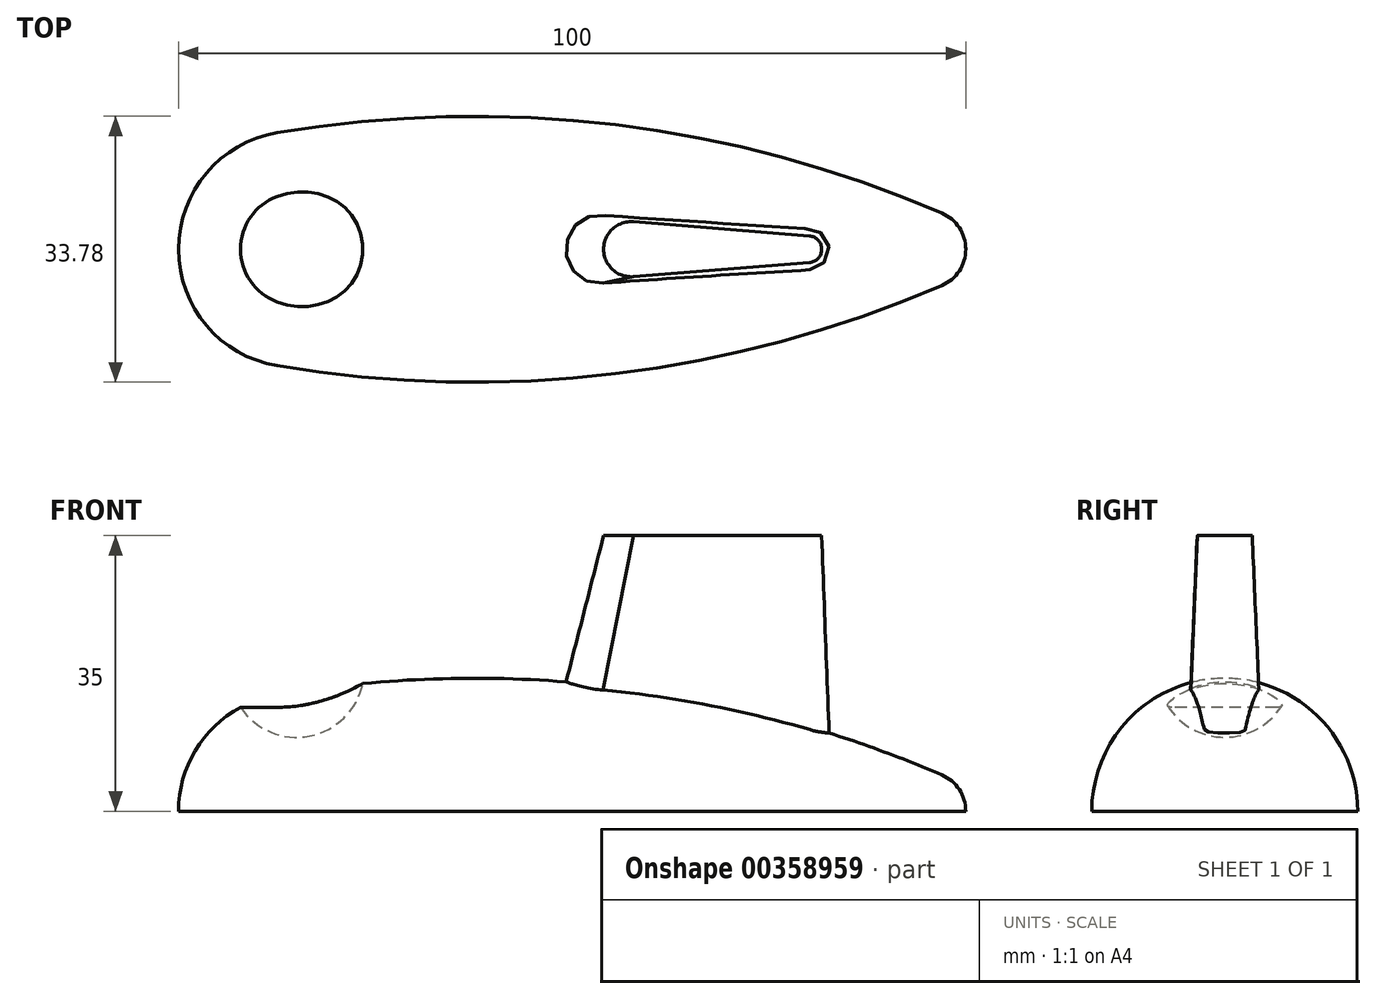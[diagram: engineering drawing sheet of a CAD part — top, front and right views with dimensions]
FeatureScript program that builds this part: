
annotation { "Feature Type Name" : "Feature", "Feature Type Description" : "" }
export const myFeature = defineFeature(function(context is Context, id is Id, definition is map)
    precondition{}
    {
        {
            var Q0;
            Q0=qCreatedBy(makeId("Top.planeOp"),FACE);
            var sketch = newSketch(context, id + "F0", { "sketchPlane" : qUnion([Q0])});
            skArc(sketch, "E0", {"start": v(-2.5, 14.8) * mm, "mid": v(-11.46, 9.68) * mm, "end": v(-15, 0) * mm});
            skArc(sketch, "E1", {"start": v(85, 0) * mm, "mid": v(84.18, 2.75) * mm, "end": v(81.98, 4.6) * mm});
            skArc(sketch, "E2", {"start": v(81.98, 4.6) * mm, "mid": v(40.48, 15.8) * mm, "end": v(-2.5, 14.8) * mm});
            skLineSegment(sketch, "E3", {"start": v(-15, 0) * mm, "end": v(85, 0) * mm});
            skPoint(sketch, "E4.orphan", {"position": v(-20.4, 0) * mm});
            skSolve(sketch);
        }
        {
            var Q0;
            Q0=makeQuery(id+"F0.imprint","IMPRINT",FACE,{"disambiguationData":[TD([[makeQuery(id+"F0.imprint","IMPRINT",EDGE,{"derivedFrom":sQuery(id+"F0.wireOp",EDGE,"E0")}),1.0]])]});
            var Q1;
            Q1=sQuery(id+"F0.wireOp",EDGE,"E3");
            revolve(context, id + "F1", {"entities" : qUnion([Q0]), "axis" : qUnion([Q1]), "revolveType" : RevolveType.ONE_DIRECTION, "angle" : 180 * degree});
        }
        {
            var Q0;
            Q0=qCreatedBy(makeId("Front.planeOp"),FACE);
            var sketch = newSketch(context, id + "F2", { "sketchPlane" : qUnion([Q0])});
            skArc(sketch, "E5", {"start": v(-8.6, 18) * mm, "mid": v(0, 9.4) * mm, "end": v(8.6, 18) * mm});
            skLineSegment(sketch, "E6", {"start": v(-8.6, 18) * mm, "end": v(8.6, 18) * mm});
            skPoint(sketch, "E7.orphan", {"position": v(-12.54, 18) * mm});
            skSolve(sketch);
        }
        {
            var Q0;
            Q0 = qSketchRegion(id + "F2", true);
            var Q1;
            Q1=sQuery(id+"F2.wireOp",EDGE,"E6");
            revolve(context, id + "F3", {"operationType" : NewBodyOperationType.REMOVE, "entities" : qUnion([Q0]), "axis" : qUnion([Q1]), "revolveType" : RevolveType.FULL, "oppositeDirection" : true});
        }
        {
            var Q0;
            Q0=qCreatedBy(makeId("Top.planeOp"),FACE);
            var sketch = newSketch(context, id + "F4", { "sketchPlane" : qUnion([Q0])});
            skArc(sketch, "E8", {"start": v(35.33, 4.99) * mm, "mid": v(30, -0.26) * mm, "end": v(35.86, -4.93) * mm});
            skArc(sketch, "E9", {"start": v(65.2, -3) * mm, "mid": v(68, 0) * mm, "end": v(65.2, 3) * mm});
            skLineSegment(sketch, "E10", {"start": v(35.33, 4.99) * mm, "end": v(65.2, 3) * mm});
            skLineSegment(sketch, "E11", {"start": v(35.86, -4.93) * mm, "end": v(65.2, -3) * mm});
            skSolve(sketch);
        }
        {
            var Q0;
            Q0=qCreatedBy(makeId("Top.planeOp"),FACE);
            cPlane(context, id + "F5", {"entities" : qUnion([Q0]), "cplaneType" : CPlaneType.OFFSET, "offset" : 35 * mm, "width" : 150 * mm, "height" : 150 * mm});
        }
        {
            var Q0;
            Q0=qCreatedBy(id+"F5.planeOp",FACE);
            var sketch = newSketch(context, id + "F6", { "sketchPlane" : qUnion([Q0])});
            skArc(sketch, "E12", {"start": v(42.78, 3.49) * mm, "mid": v(39, 0) * mm, "end": v(42.78, -3.49) * mm});
            skArc(sketch, "E13", {"start": v(65.14, -1.7) * mm, "mid": v(66.7, 0) * mm, "end": v(65.14, 1.7) * mm});
            skLineSegment(sketch, "E14", {"start": v(42.78, 3.49) * mm, "end": v(65.14, 1.7) * mm});
            skLineSegment(sketch, "E15", {"start": v(42.78, -3.49) * mm, "end": v(65.14, -1.7) * mm});
            skSolve(sketch);
        }
        {
            var Q1;
            Q1 = qSketchRegion(id + "F4", true);
            var Q2;
            Q2 = qSketchRegion(id + "F6", true);
            loft(context, id + "F7", {"operationType" : NewBodyOperationType.ADD, "sheetProfilesArray" : [{ "sheetProfileEntities" : qUnion([Q1]) }, { "sheetProfileEntities" : qUnion([Q2]) }]});
        }
    });
